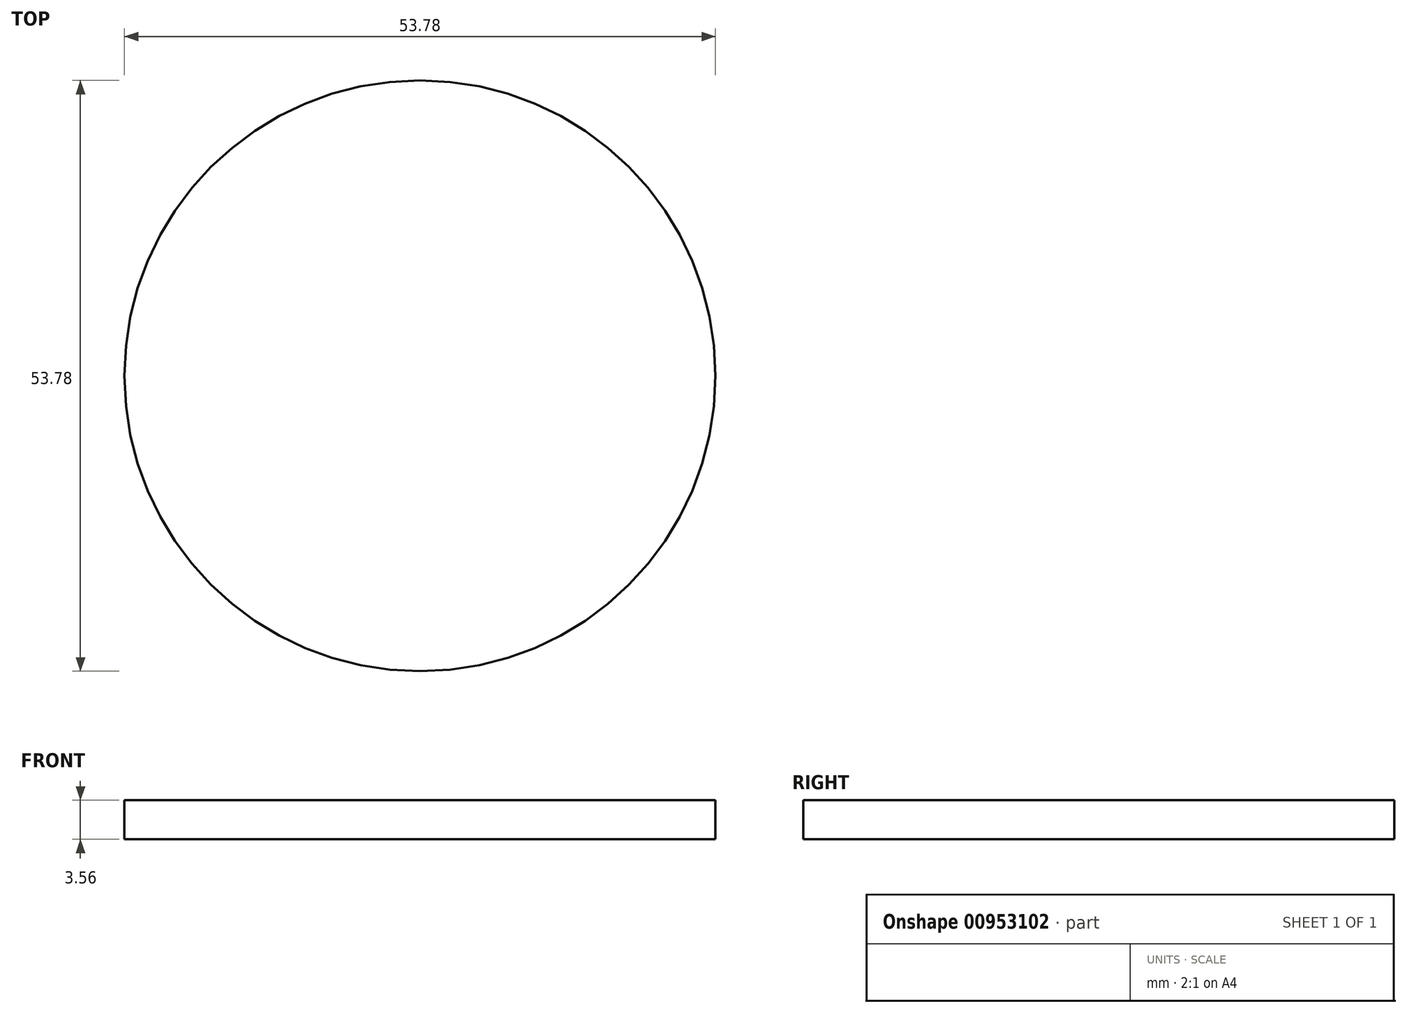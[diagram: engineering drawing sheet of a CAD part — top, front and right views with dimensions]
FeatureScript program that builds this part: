
annotation { "Feature Type Name" : "Feature", "Feature Type Description" : "" }
export const myFeature = defineFeature(function(context is Context, id is Id, definition is map)
    precondition{}
    {
        {
            var Q0;
            Q0=qCreatedBy(makeId("Top.planeOp"),FACE);
            var sketch = newSketch(context, id + "F0", { "sketchPlane" : qUnion([Q0])});
            skCircle(sketch, "E0", {"center": v(0, 0) * mm, "radius": 26.9 * mm});
            skSolve(sketch);
        }
        {
            var Q0;
            Q0=makeQuery(id+"F0.imprint","IMPRINT",FACE,{"disambiguationData":[TD([[makeQuery(id+"F0.imprint","IMPRINT",EDGE,{"derivedFrom":sQuery(id+"F0.wireOp",EDGE,"E0")}),1.0]])]});
            extrude(context, id + "F1", {"entities" : qUnion([Q0]), "depth" : 3.56 * mm, "offsetDistance" : 25.4 * mm});
        }
    });
